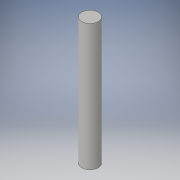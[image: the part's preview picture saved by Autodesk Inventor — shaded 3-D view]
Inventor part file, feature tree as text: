
AUTODESK INVENTOR PART (.ipt)
format: ipt  version: 2016 (Build 200138000, 138)  size: 84,992 bytes
history: native  units: in
note: dims shown in document units (in); Inventor stores cm internally (conversion verified against a paired STEP export)
features: extrude x1, sketch x1
ambient origin geometry x8: Origin, YZ Plane, XZ Plane, XY Plane, X Axis, Y Axis, Z Axis, Center Point
bodies: Solid1 (feature_tree)
feature tree (2):
  extrude  "Extrusion1"  Depth=1.825in TaperAngle=0.0deg
  sketch  "Sketch1"  dims[d0=0.2362in d1=1.825in d2=0.0in]
